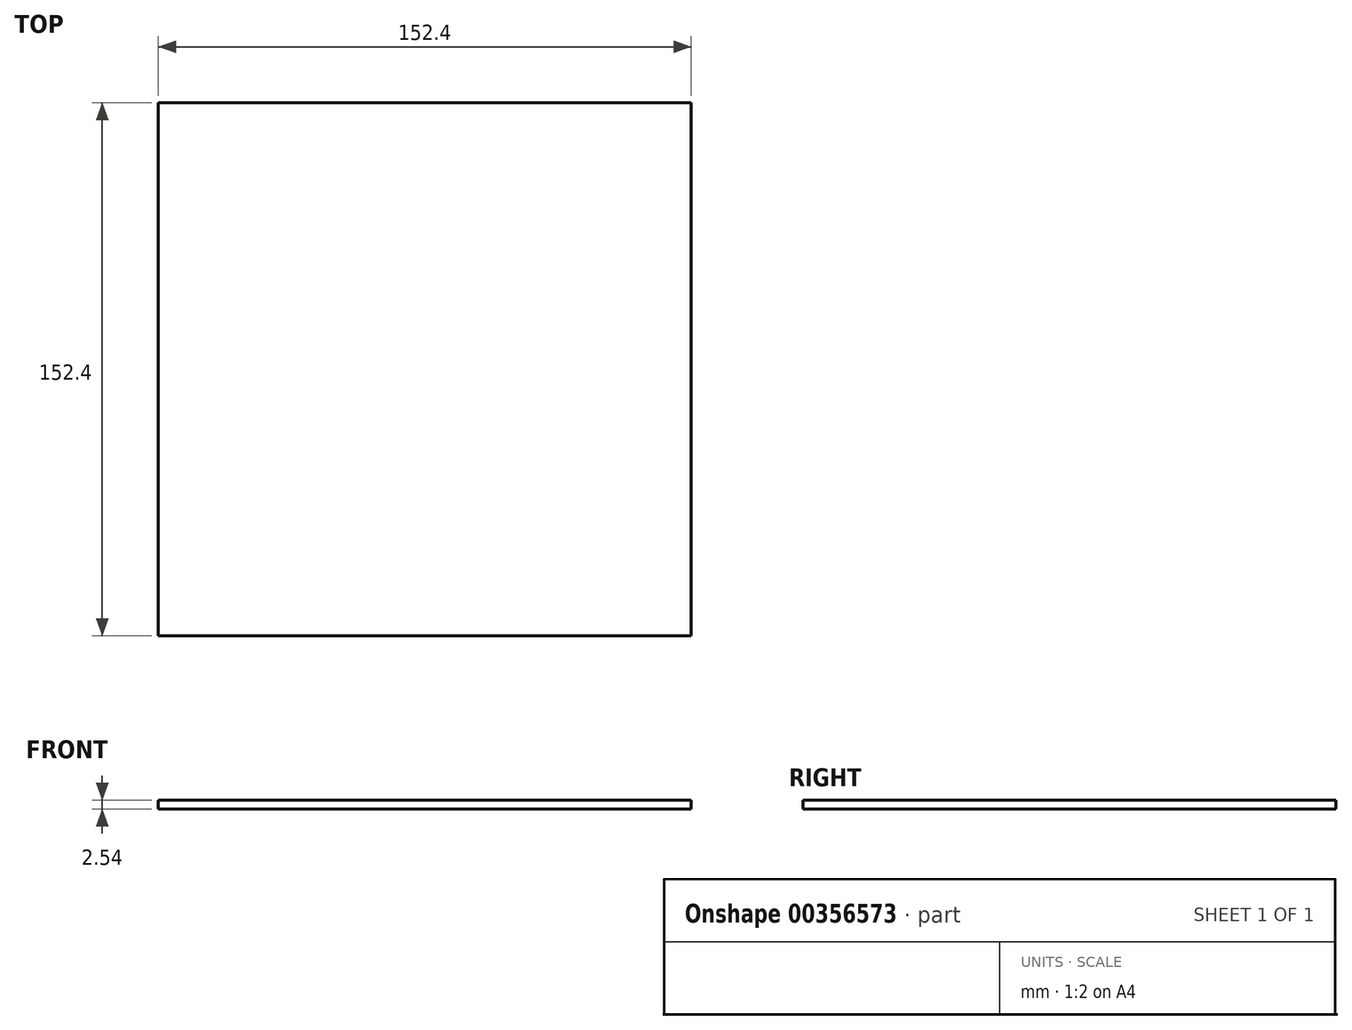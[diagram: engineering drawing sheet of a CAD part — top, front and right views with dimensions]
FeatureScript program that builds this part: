
annotation { "Feature Type Name" : "Feature", "Feature Type Description" : "" }
export const myFeature = defineFeature(function(context is Context, id is Id, definition is map)
    precondition{}
    {
        {
            var Q0;
            Q0=qCreatedBy(makeId("Top.planeOp"),FACE);
            var sketch = newSketch(context, id + "F0", { "sketchPlane" : qUnion([Q0])});
            skLineSegment(sketch, "E0.bottom", {"start": v(-78.75, 72.2) * mm, "end": v(73.65, 72.2) * mm});
            skLineSegment(sketch, "E0.top", {"start": v(-78.75, -80.2) * mm, "end": v(73.65, -80.2) * mm});
            skLineSegment(sketch, "E0.left", {"start": v(-78.75, 72.2) * mm, "end": v(-78.75, -80.2) * mm});
            skLineSegment(sketch, "E0.right", {"start": v(73.65, 72.2) * mm, "end": v(73.65, -80.2) * mm});
            skSolve(sketch);
        }
        {
            var Q0;
            Q0=makeQuery(id+"F0.imprint","IMPRINT",FACE,{"disambiguationData":[TD([[makeQuery(id+"F0.imprint","IMPRINT",EDGE,{"derivedFrom":sQuery(id+"F0.wireOp",EDGE,"E0.bottom")}),-1.0]])]});
            extrude(context, id + "F1", {"entities" : qUnion([Q0]), "depth" : 2.54 * mm, "offsetDistance" : 25.4 * mm});
        }
    });
